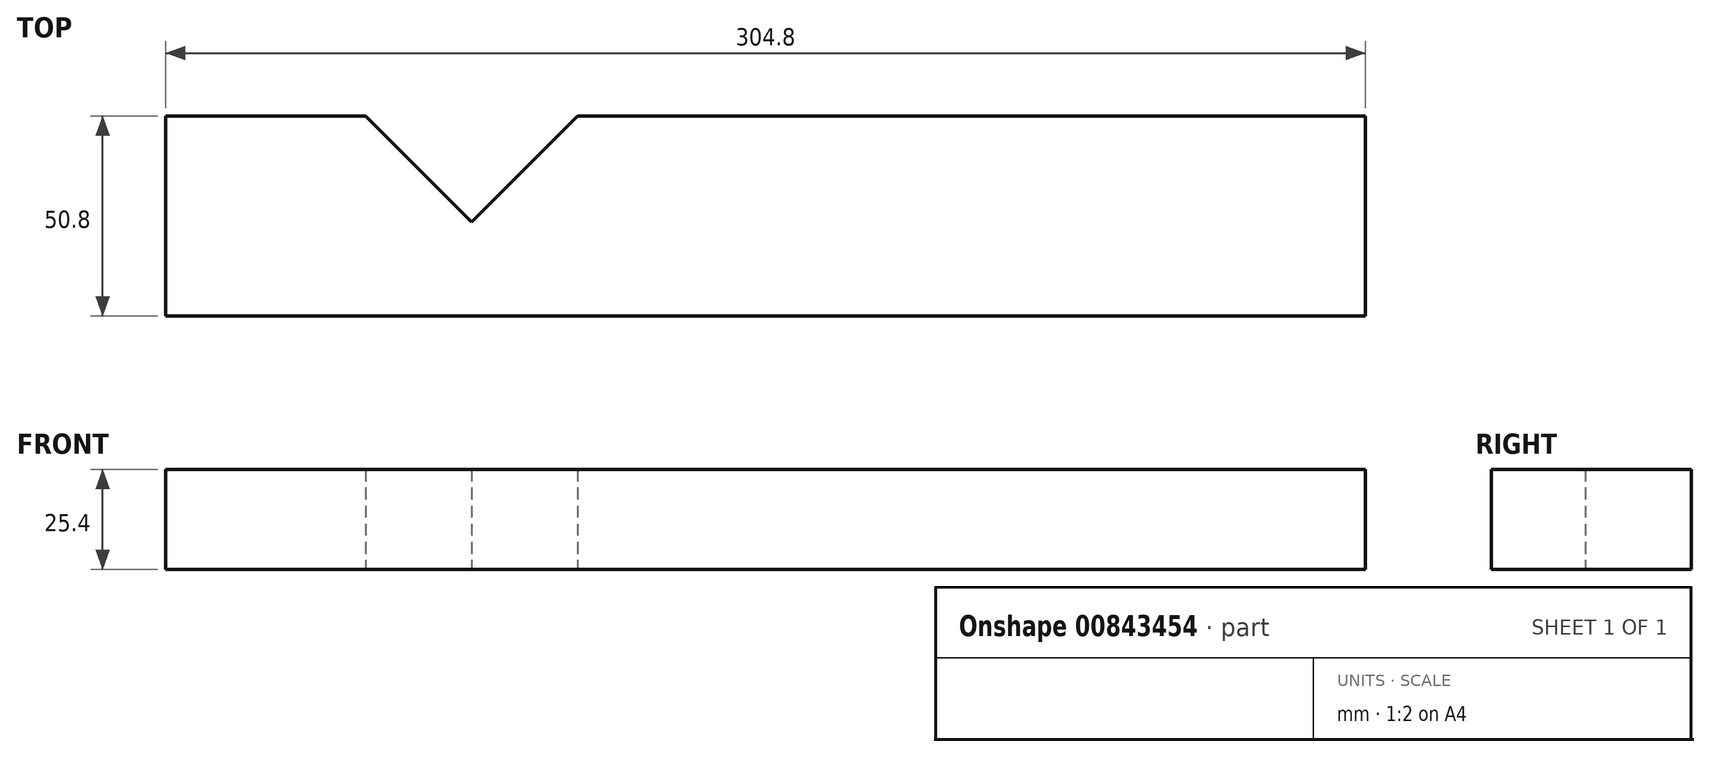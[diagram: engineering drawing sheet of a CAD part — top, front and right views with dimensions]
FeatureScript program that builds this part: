
annotation { "Feature Type Name" : "Feature", "Feature Type Description" : "" }
export const myFeature = defineFeature(function(context is Context, id is Id, definition is map)
    precondition{}
    {
        {
            var Q0;
            Q0=qCreatedBy(makeId("Top.planeOp"),FACE);
            var sketch = newSketch(context, id + "F0", { "sketchPlane" : qUnion([Q0])});
            skLineSegment(sketch, "E0", {"start": v(-91.3, -210.46) * mm, "end": v(-91.3, 94.34) * mm, "construction": true});
            skLineSegment(sketch, "E1", {"start": v(-91.3, 94.34) * mm, "end": v(213.5, 94.34) * mm, "construction": true});
            skLineSegment(sketch, "E2", {"start": v(213.5, 94.34) * mm, "end": v(213.5, 18.14) * mm, "construction": true});
            skLineSegment(sketch, "E3", {"start": v(213.5, 18.14) * mm, "end": v(-15.1, 18.14) * mm, "construction": true});
            skLineSegment(sketch, "E4", {"start": v(-15.1, 18.14) * mm, "end": v(-15.1, -210.46) * mm, "construction": true});
            skLineSegment(sketch, "E5", {"start": v(-15.1, -210.46) * mm, "end": v(-91.3, -210.46) * mm, "construction": true});
            skSolve(sketch);
        }
        {
            var Q0;
            Q0=qCreatedBy(makeId("Top.planeOp"),FACE);
            var sketch = newSketch(context, id + "F1", { "sketchPlane" : qUnion([Q0])});
            skLineSegment(sketch, "E6.bottom", {"start": v(213.5, 94.34) * mm, "end": v(-91.3, 94.34) * mm});
            skLineSegment(sketch, "E6.top", {"start": v(213.5, 145.14) * mm, "end": v(13.38, 145.14) * mm});
            skLineSegment(sketch, "E6.left", {"start": v(213.5, 94.34) * mm, "end": v(213.5, 145.14) * mm});
            skLineSegment(sketch, "E6.right", {"start": v(-91.3, 94.34) * mm, "end": v(-91.3, 145.14) * mm});
            skLineSegment(sketch, "E7", {"start": v(-40.5, 145.14) * mm, "end": v(-13.56, 118.2) * mm});
            skLineSegment(sketch, "E8", {"start": v(-13.56, 118.2) * mm, "end": v(13.38, 145.14) * mm});
            skLineSegment(sketch, "E9.trimOffspring", {"start": v(-40.5, 145.14) * mm, "end": v(-91.3, 145.14) * mm});
            skSolve(sketch);
        }
        {
            var Q0;
            Q0 = qSketchRegion(id + "F1", true);
            extrude(context, id + "F2", {"entities" : qUnion([Q0]), "depth" : 25.4 * mm, "offsetDistance" : 25.4 * mm});
        }
    });
